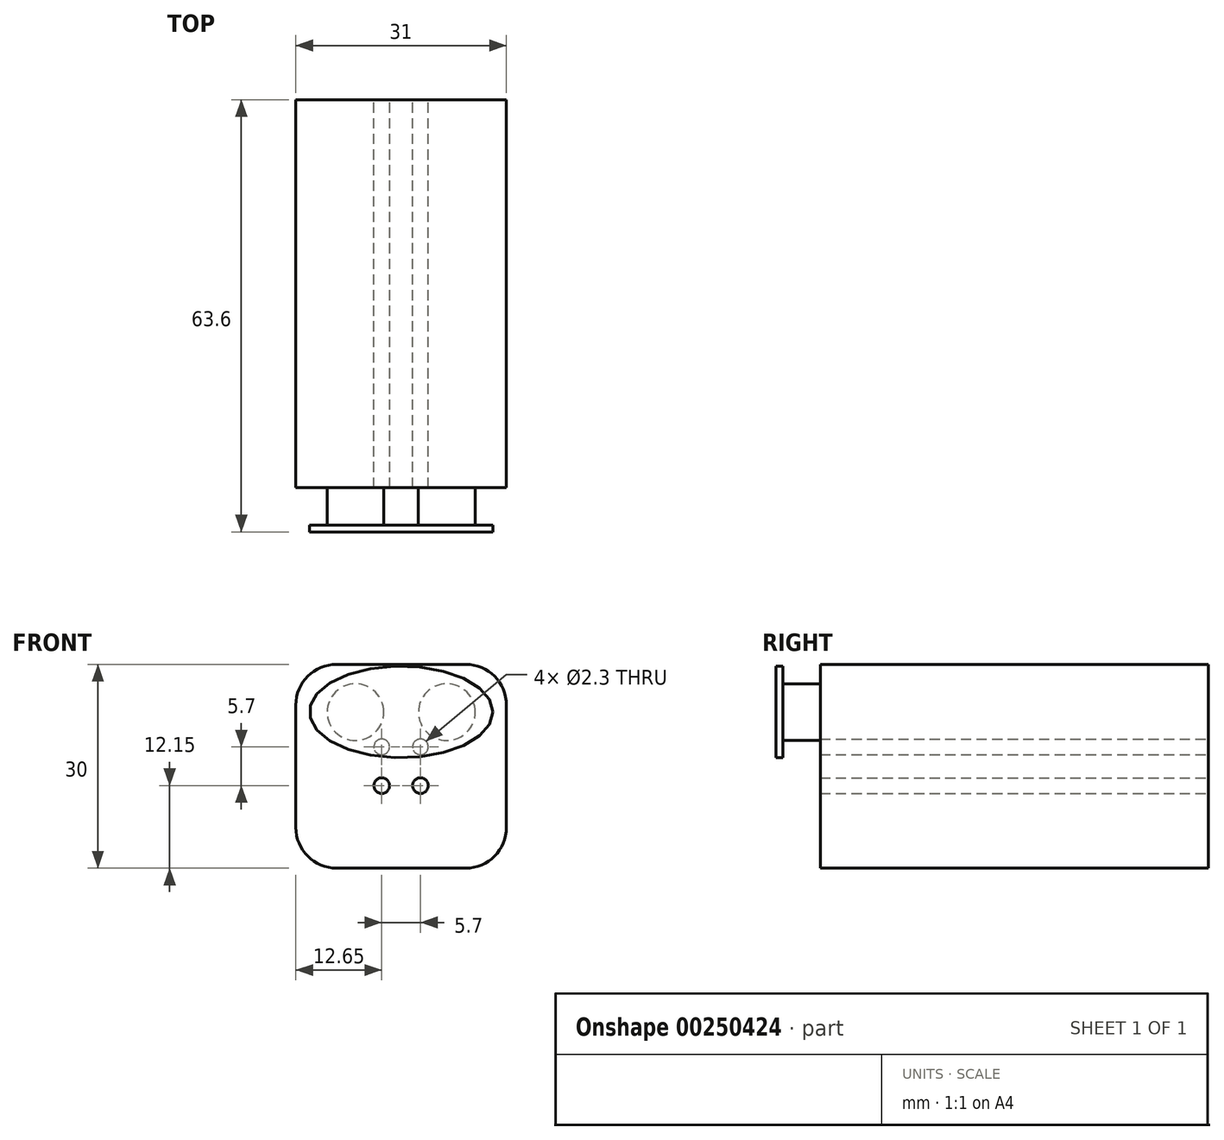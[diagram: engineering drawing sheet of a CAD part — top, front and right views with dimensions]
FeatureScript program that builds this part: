
annotation { "Feature Type Name" : "Feature", "Feature Type Description" : "" }
export const myFeature = defineFeature(function(context is Context, id is Id, definition is map)
    precondition{}
    {
        {
            var Q0;
            Q0=qCreatedBy(makeId("Front.planeOp"),FACE);
            var sketch = newSketch(context, id + "F0", { "sketchPlane" : qUnion([Q0])});
            skLineSegment(sketch, "E0.bottom", {"start": v(15.5, -15) * mm, "end": v(-15.5, -15) * mm});
            skLineSegment(sketch, "E0.top", {"start": v(15.5, 15) * mm, "end": v(-15.5, 15) * mm});
            skLineSegment(sketch, "E0.left", {"start": v(15.5, -15) * mm, "end": v(15.5, 15) * mm});
            skLineSegment(sketch, "E0.right", {"start": v(-15.5, -15) * mm, "end": v(-15.5, 15) * mm});
            skPoint(sketch, "E0.middle", {"position": v(0, 0) * mm});
            skSolve(sketch);
        }
        {
            var Q0;
            Q0 = qSketchRegion(id + "F0", true);
            extrude(context, id + "F1", {"entities" : qUnion([Q0]), "endBound" : BoundingType.SYMMETRIC, "depth" : 57.1 * mm});
        }
        {
            var Q0;
            Q0=makeQuery(id+"F1.opExtrude","CAP_FACE",FACE,{"disambiguationData":[OSD([sQuery(id+"F0.wireOp",EDGE,"E0.bottom"),sQuery(id+"F0.wireOp",EDGE,"E0.top"),sQuery(id+"F0.wireOp",EDGE,"E0.left"),sQuery(id+"F0.wireOp",EDGE,"E0.right")])],"isStart":true});
            var sketch = newSketch(context, id + "F2", { "sketchPlane" : qUnion([Q0])});
            skCircle(sketch, "E1", {"center": v(-2.85, 2.85) * mm, "radius": 1.15 * mm});
            skCircle(sketch, "E2", {"center": v(-2.85, -2.85) * mm, "radius": 1.15 * mm});
            skCircle(sketch, "E3", {"center": v(2.85, 2.85) * mm, "radius": 1.15 * mm});
            skCircle(sketch, "E4", {"center": v(2.85, -2.85) * mm, "radius": 1.15 * mm});
            skLineSegment(sketch, "E5", {"start": v(-2.85, 2.85) * mm, "end": v(0, 2.85) * mm, "construction": true});
            skLineSegment(sketch, "E6", {"start": v(0, 2.85) * mm, "end": v(2.85, 2.85) * mm, "construction": true});
            skLineSegment(sketch, "E7", {"start": v(-2.85, 2.85) * mm, "end": v(-2.85, 0) * mm, "construction": true});
            skLineSegment(sketch, "E8", {"start": v(-2.85, 0) * mm, "end": v(-2.85, -2.85) * mm, "construction": true});
            skLineSegment(sketch, "E9", {"start": v(-2.85, -2.85) * mm, "end": v(0, -2.85) * mm, "construction": true});
            skLineSegment(sketch, "E10", {"start": v(0, -2.85) * mm, "end": v(2.85, -2.85) * mm, "construction": true});
            skLineSegment(sketch, "E11", {"start": v(2.85, 2.85) * mm, "end": v(2.85, 0) * mm, "construction": true});
            skLineSegment(sketch, "E12", {"start": v(2.85, 0) * mm, "end": v(2.85, -2.85) * mm, "construction": true});
            skSolve(sketch);
        }
        {
            var Q0;
            Q0=makeQuery(id+"F2.imprint","IMPRINT",FACE,{"disambiguationData":[TD([[makeQuery(id+"F2.imprint","IMPRINT",EDGE,{"derivedFrom":sQuery(id+"F2.wireOp",EDGE,"E1")}),1.0]])]});
            var Q1;
            Q1=makeQuery(id+"F2.imprint","IMPRINT",FACE,{"disambiguationData":[TD([[makeQuery(id+"F2.imprint","IMPRINT",EDGE,{"derivedFrom":sQuery(id+"F2.wireOp",EDGE,"E3")}),1.0]])]});
            var Q2;
            Q2=makeQuery(id+"F2.imprint","IMPRINT",FACE,{"disambiguationData":[TD([[makeQuery(id+"F2.imprint","IMPRINT",EDGE,{"derivedFrom":sQuery(id+"F2.wireOp",EDGE,"E2")}),1.0]])]});
            var Q3;
            Q3=makeQuery(id+"F2.imprint","IMPRINT",FACE,{"disambiguationData":[TD([[makeQuery(id+"F2.imprint","IMPRINT",EDGE,{"derivedFrom":sQuery(id+"F2.wireOp",EDGE,"E4")}),1.0]])]});
            extrude(context, id + "F3", {"entities" : qUnion([Q0, Q1, Q2, Q3]), "operationType" : NewBodyOperationType.REMOVE, "endBound" : BoundingType.THROUGH_ALL, "oppositeDirection" : true, "depth" : 100 * mm});
        }
        {
            var Q0;
            Q0=makeQuery(id+"F1.opExtrude","CAP_FACE",FACE,{"disambiguationData":[OSD([sQuery(id+"F0.wireOp",EDGE,"E0.bottom"),sQuery(id+"F0.wireOp",EDGE,"E0.top"),sQuery(id+"F0.wireOp",EDGE,"E0.left"),sQuery(id+"F0.wireOp",EDGE,"E0.right")])],"isStart":false});
            var sketch = newSketch(context, id + "F4", { "sketchPlane" : qUnion([Q0])});
            skCircle(sketch, "E13", {"center": v(6.72, 7.96) * mm, "radius": 4.17 * mm});
            skCircle(sketch, "E14", {"center": v(-6.73, 7.96) * mm, "radius": 4.17 * mm});
            skSolve(sketch);
        }
        {
            var Q0;
            Q0 = qSketchRegion(id + "F4", true);
            extrude(context, id + "F5", {"entities" : qUnion([Q0]), "operationType" : NewBodyOperationType.ADD, "depth" : 5.5 * mm});
        }
        {
            var Q0;
            Q0=makeQuery(id+"F5.opExtrude","CAP_FACE",FACE,{"disambiguationData":[OSD([sQuery(id+"F4.wireOp",EDGE,"E14")])],"isStart":false});
            var sketch = newSketch(context, id + "F6", { "sketchPlane" : qUnion([Q0])});
            skEllipse(sketch, "E15", {"center": v(0, 8) * mm, "majorRadius": 13.5 * mm, "minorRadius": 6.75 * mm, "majorAxis": v(1, 0)});
            skSolve(sketch);
        }
        {
            var Q0;
            Q0 = qSketchRegion(id + "F6", true);
            extrude(context, id + "F7", {"entities" : qUnion([Q0]), "operationType" : NewBodyOperationType.ADD, "depth" : 1 * mm});
        }
        {
            var Q0;
            Q0=makeQuery(id+"F1.opExtrude","SWEPT_EDGE",EDGE,{"disambiguationData":[OSD([sQuery(id+"F0.wireOp",EDGE,"E0.top"),sQuery(id+"F0.wireOp",EDGE,"E0.right")])]});
            var Q1;
            Q1=makeQuery(id+"F1.opExtrude","SWEPT_EDGE",EDGE,{"disambiguationData":[OSD([sQuery(id+"F0.wireOp",EDGE,"E0.top"),sQuery(id+"F0.wireOp",EDGE,"E0.left")])]});
            var Q2;
            Q2=makeQuery(id+"F1.opExtrude","SWEPT_EDGE",EDGE,{"disambiguationData":[OSD([sQuery(id+"F0.wireOp",EDGE,"E0.bottom"),sQuery(id+"F0.wireOp",EDGE,"E0.right")])]});
            var Q3;
            Q3=makeQuery(id+"F1.opExtrude","SWEPT_EDGE",EDGE,{"disambiguationData":[OSD([sQuery(id+"F0.wireOp",EDGE,"E0.bottom"),sQuery(id+"F0.wireOp",EDGE,"E0.left")])]});
            fillet(context, id + "F8", {"entities" : qUnion([Q0, Q1, Q2, Q3]), "radius" : 6 * mm, "tangentPropagation" : true, "allowEdgeOverflow" : false});
        }
    });
